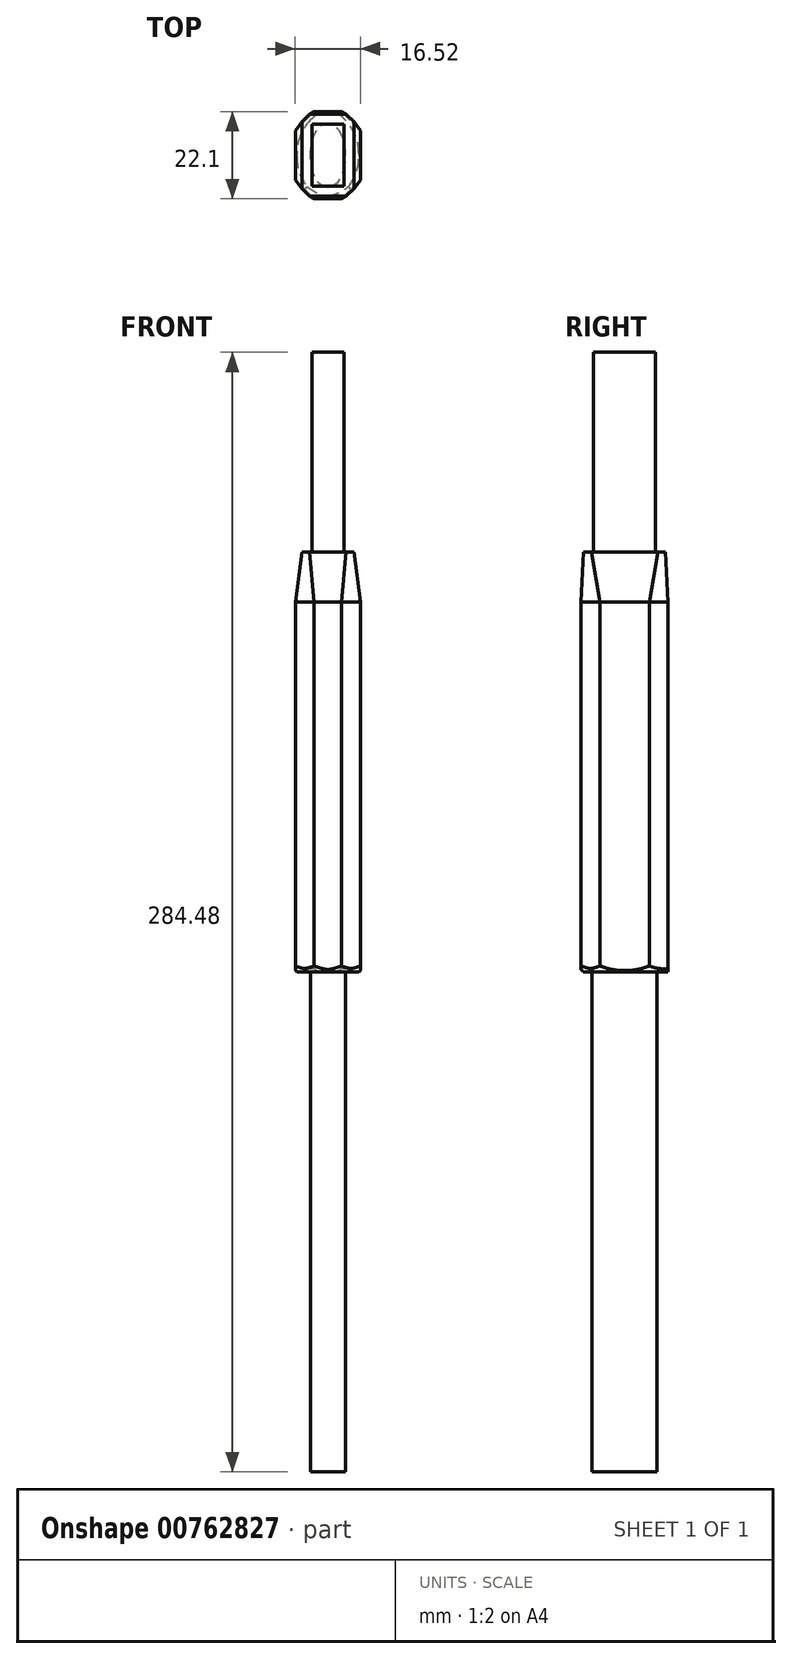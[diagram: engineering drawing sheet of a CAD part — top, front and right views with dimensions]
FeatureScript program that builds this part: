
annotation { "Feature Type Name" : "Feature", "Feature Type Description" : "" }
export const myFeature = defineFeature(function(context is Context, id is Id, definition is map)
    precondition{}
    {
        {
            var Q0;
            Q0=qCreatedBy(makeId("Top.planeOp"),FACE);
            var sketch = newSketch(context, id + "F0", { "sketchPlane" : qUnion([Q0])});
            skLineSegment(sketch, "E0.bottom", {"start": v(-8.26, -11.05) * mm, "end": v(8.26, -11.05) * mm});
            skLineSegment(sketch, "E0.top", {"start": v(-8.26, 11.05) * mm, "end": v(8.26, 11.05) * mm});
            skLineSegment(sketch, "E0.left", {"start": v(-8.26, -11.05) * mm, "end": v(-8.26, 11.05) * mm});
            skLineSegment(sketch, "E0.right", {"start": v(8.26, -11.05) * mm, "end": v(8.26, 11.05) * mm});
            skPoint(sketch, "E0.middle", {"position": v(0, 0) * mm});
            skLineSegment(sketch, "E1", {"start": v(-8.26, 6.3) * mm, "end": v(-3.5, 11.05) * mm});
            skLineSegment(sketch, "E2", {"start": v(-3.5, 11.05) * mm, "end": v(3.5, 11.05) * mm});
            skLineSegment(sketch, "E3", {"start": v(3.5, 11.05) * mm, "end": v(8.26, 6.3) * mm});
            skLineSegment(sketch, "E4", {"start": v(-8.26, -6.3) * mm, "end": v(-3.5, -11.05) * mm});
            skLineSegment(sketch, "E5", {"start": v(3.5, -11.05) * mm, "end": v(8.26, -6.3) * mm});
            skSolve(sketch);
        }
        {
            var Q0;
            {var subQ3=sQuery(id+"F0.wireOp",EDGE,"E1");Q0=makeQuery(id+"F0.imprint","IMPRINT",FACE,{"disambiguationData":[TD([[makeQuery(id+"F0.imprint","IMPRINT",EDGE,{"derivedFrom":subQ3}),-1.0]])]});}
            extrude(context, id + "F1", {"entities" : qUnion([Q0]), "depth" : 93.98 * mm, "offsetDistance" : 25.4 * mm});
        }
        {
            var Q0;
            Q0=makeQuery(id+"F1.opExtrude","CAP_FACE",FACE,{"disambiguationData":[OSD([sQuery(id+"F0.wireOp",EDGE,"E0.bottom"),sQuery(id+"F0.wireOp",EDGE,"E0.left"),sQuery(id+"F0.wireOp",EDGE,"E0.right"),sQuery(id+"F0.wireOp",EDGE,"E1"),sQuery(id+"F0.wireOp",EDGE,"E2"),sQuery(id+"F0.wireOp",EDGE,"E3"),sQuery(id+"F0.wireOp",EDGE,"E4"),sQuery(id+"F0.wireOp",EDGE,"E5")])],"isStart":false});
            cPlane(context, id + "F2", {"entities" : qUnion([Q0]), "cplaneType" : CPlaneType.OFFSET, "offset" : 12.7 * mm, "width" : 152.4 * mm, "height" : 152.4 * mm});
        }
        {
            var Q0;
            Q0=qCreatedBy(id+"F2.planeOp",FACE);
            var sketch = newSketch(context, id + "F3", { "sketchPlane" : qUnion([Q0])});
            skLineSegment(sketch, "E6.bottom", {"start": v(-6.6, -10.41) * mm, "end": v(6.6, -10.41) * mm});
            skLineSegment(sketch, "E6.top", {"start": v(-6.6, 10.41) * mm, "end": v(6.6, 10.41) * mm});
            skLineSegment(sketch, "E6.left", {"start": v(-6.6, -10.41) * mm, "end": v(-6.6, 10.41) * mm});
            skLineSegment(sketch, "E6.right", {"start": v(6.6, -10.41) * mm, "end": v(6.6, 10.41) * mm});
            skPoint(sketch, "E6.middle", {"position": v(0, 0) * mm});
            skLineSegment(sketch, "E7", {"start": v(4.67, 10.41) * mm, "end": v(6.6, 8.48) * mm});
            skLineSegment(sketch, "E8", {"start": v(-6.6, 8.48) * mm, "end": v(-4.67, 10.41) * mm});
            skLineSegment(sketch, "E9", {"start": v(-6.6, -8.48) * mm, "end": v(-4.67, -10.41) * mm});
            skLineSegment(sketch, "E10", {"start": v(4.67, -10.41) * mm, "end": v(6.6, -8.48) * mm});
            skSolve(sketch);
        }
        {
            var Q1;
            {var subQ0=sQuery(id+"F3.wireOp",EDGE,"E7");Q1=makeQuery(id+"F3.imprint","IMPRINT",FACE,{"disambiguationData":[TD([[makeQuery(id+"F3.imprint","IMPRINT",EDGE,{"derivedFrom":subQ0}),-1.0]])]});}
            var Q2;
            Q2=makeQuery(id+"F1.opExtrude","CAP_FACE",FACE,{"disambiguationData":[OSD([sQuery(id+"F0.wireOp",EDGE,"E0.bottom"),sQuery(id+"F0.wireOp",EDGE,"E0.left"),sQuery(id+"F0.wireOp",EDGE,"E0.right"),sQuery(id+"F0.wireOp",EDGE,"E1"),sQuery(id+"F0.wireOp",EDGE,"E2"),sQuery(id+"F0.wireOp",EDGE,"E3"),sQuery(id+"F0.wireOp",EDGE,"E4"),sQuery(id+"F0.wireOp",EDGE,"E5")])],"isStart":false});
            loft(context, id + "F4", {"operationType" : NewBodyOperationType.ADD, "sheetProfilesArray" : [{ "sheetProfileEntities" : qUnion([Q1]) }, { "sheetProfileEntities" : qUnion([Q2]) }]});
        }
        {
            var Q0;
            {var subQ0=sQuery(id+"F3.wireOp",EDGE,"E7");Q0=makeQuery(id+"F4.opLoft","CAP_FACE",FACE,{"disambiguationData":[OSD([makeQuery(id+"F3.imprint","IMPRINT",FACE,{"disambiguationData":[TD([[makeQuery(id+"F3.imprint","IMPRINT",EDGE,{"derivedFrom":subQ0}),-1.0]])]})])],"isStart":true});}
            var sketch = newSketch(context, id + "F5", { "sketchPlane" : qUnion([Q0])});
            skLineSegment(sketch, "E11.bottom", {"start": v(-4.06, -7.87) * mm, "end": v(4.06, -7.87) * mm});
            skLineSegment(sketch, "E11.top", {"start": v(-4.06, 7.87) * mm, "end": v(4.06, 7.87) * mm});
            skLineSegment(sketch, "E11.left", {"start": v(-4.06, -7.87) * mm, "end": v(-4.06, 7.87) * mm});
            skLineSegment(sketch, "E11.right", {"start": v(4.06, -7.87) * mm, "end": v(4.06, 7.87) * mm});
            skPoint(sketch, "E11.middle", {"position": v(0, 0) * mm});
            skSolve(sketch);
        }
        {
            var Q0;
            Q0=makeQuery(id+"F5.imprint","IMPRINT",FACE,{"disambiguationData":[TD([[makeQuery(id+"F5.imprint","IMPRINT",EDGE,{"derivedFrom":sQuery(id+"F5.wireOp",EDGE,"E11.bottom")}),1.0]])]});
            extrude(context, id + "F6", {"entities" : qUnion([Q0]), "operationType" : NewBodyOperationType.ADD, "depth" : 50.8 * mm, "offsetDistance" : 25.4 * mm});
        }
        {
            var Q0;
            Q0=makeQuery(id+"F1.opExtrude","CAP_FACE",FACE,{"disambiguationData":[OSD([sQuery(id+"F0.wireOp",EDGE,"E0.bottom"),sQuery(id+"F0.wireOp",EDGE,"E0.left"),sQuery(id+"F0.wireOp",EDGE,"E0.right"),sQuery(id+"F0.wireOp",EDGE,"E1"),sQuery(id+"F0.wireOp",EDGE,"E2"),sQuery(id+"F0.wireOp",EDGE,"E3"),sQuery(id+"F0.wireOp",EDGE,"E4"),sQuery(id+"F0.wireOp",EDGE,"E5")])],"isStart":true});
            var sketch = newSketch(context, id + "F7", { "sketchPlane" : qUnion([Q0])});
            skEllipse(sketch, "E12", {"center": v(0, 0) * mm, "majorRadius": 8.26 * mm, "minorRadius": 4.45 * mm, "majorAxis": v(0, 1)});
            skSolve(sketch);
        }
        {
            var Q0;
            Q0=makeQuery(id+"F7.imprint","IMPRINT",FACE,{"disambiguationData":[TD([[makeQuery(id+"F7.imprint","IMPRINT",EDGE,{"derivedFrom":sQuery(id+"F7.wireOp",EDGE,"E12")}),1.0]])]});
            extrude(context, id + "F8", {"entities" : qUnion([Q0]), "operationType" : NewBodyOperationType.ADD, "depth" : 127 * mm, "offsetDistance" : 25.4 * mm});
        }
        {
            var Q0;
            Q0=makeQuery(id+"F1.opExtrude","CAP_EDGE",EDGE,{"disambiguationData":[OSD([sQuery(id+"F0.wireOp",EDGE,"E4")])],"isStart":true});
            var Q1;
            Q1=makeQuery(id+"F1.opExtrude","CAP_EDGE",EDGE,{"disambiguationData":[OSD([sQuery(id+"F0.wireOp",EDGE,"E5")])],"isStart":true});
            var Q2;
            Q2=makeQuery(id+"F1.opExtrude","CAP_EDGE",EDGE,{"disambiguationData":[OSD([sQuery(id+"F0.wireOp",EDGE,"E1")])],"isStart":true});
            var Q3;
            Q3=makeQuery(id+"F1.opExtrude","CAP_EDGE",EDGE,{"disambiguationData":[OSD([sQuery(id+"F0.wireOp",EDGE,"E3")])],"isStart":true});
            chamfer(context, id + "F9", {"entities" : qUnion([Q0, Q1, Q2, Q3]), "width" : 0.84 * mm, "tangentPropagation" : true});
        }
        {
            var Q0;
            Q0=makeQuery(id+"F1.opExtrude","CAP_EDGE",EDGE,{"disambiguationData":[OSD([sQuery(id+"F0.wireOp",EDGE,"E0.bottom")])],"isStart":true});
            var Q1;
            Q1=makeQuery(id+"F1.opExtrude","CAP_EDGE",EDGE,{"disambiguationData":[OSD([sQuery(id+"F0.wireOp",EDGE,"E0.left")])],"isStart":true});
            var Q2;
            Q2=makeQuery(id+"F1.opExtrude","CAP_EDGE",EDGE,{"disambiguationData":[OSD([sQuery(id+"F0.wireOp",EDGE,"E2")])],"isStart":true});
            var Q3;
            Q3=makeQuery(id+"F1.opExtrude","CAP_EDGE",EDGE,{"disambiguationData":[OSD([sQuery(id+"F0.wireOp",EDGE,"E0.right")])],"isStart":true});
            chamfer(context, id + "F10", {"entities" : qUnion([Q0, Q1, Q2, Q3]), "width" : 0.38 * mm, "tangentPropagation" : true});
        }
        {
            var Q0;
            Q0=makeQuery(id+"F10.opChamfer","BLEND_EDGE",EDGE,{"blendedFrom":[makeQuery(id+"F1.opExtrude","CAP_EDGE",EDGE,{"disambiguationData":[OSD([sQuery(id+"F0.wireOp",EDGE,"E0.left")])],"isStart":true}),makeQuery(id+"F9.opChamfer","BLEND_FACE",FACE,{"disambiguationData":[OSD([sQuery(id+"F0.wireOp",EDGE,"E4")])]})],"blendedInto":[makeQuery(id+"F9.opChamfer","BLEND_FACE",FACE,{"disambiguationData":[OSD([sQuery(id+"F0.wireOp",EDGE,"E4")])]})]});
            var Q1;
            Q1=makeQuery(id+"F10.opChamfer","BLEND_EDGE",EDGE,{"blendedFrom":[makeQuery(id+"F1.opExtrude","CAP_EDGE",EDGE,{"disambiguationData":[OSD([sQuery(id+"F0.wireOp",EDGE,"E0.bottom")])],"isStart":true}),makeQuery(id+"F9.opChamfer","BLEND_FACE",FACE,{"disambiguationData":[OSD([sQuery(id+"F0.wireOp",EDGE,"E4")])]})],"blendedInto":[makeQuery(id+"F9.opChamfer","BLEND_FACE",FACE,{"disambiguationData":[OSD([sQuery(id+"F0.wireOp",EDGE,"E4")])]})]});
            var Q2;
            Q2=makeQuery(id+"F10.opChamfer","BLEND_EDGE",EDGE,{"blendedFrom":[makeQuery(id+"F1.opExtrude","CAP_EDGE",EDGE,{"disambiguationData":[OSD([sQuery(id+"F0.wireOp",EDGE,"E0.bottom")])],"isStart":true}),makeQuery(id+"F9.opChamfer","BLEND_FACE",FACE,{"disambiguationData":[OSD([sQuery(id+"F0.wireOp",EDGE,"E5")])]})],"blendedInto":[makeQuery(id+"F9.opChamfer","BLEND_FACE",FACE,{"disambiguationData":[OSD([sQuery(id+"F0.wireOp",EDGE,"E5")])]})]});
            var Q3;
            Q3=makeQuery(id+"F10.opChamfer","BLEND_EDGE",EDGE,{"blendedFrom":[makeQuery(id+"F1.opExtrude","CAP_EDGE",EDGE,{"disambiguationData":[OSD([sQuery(id+"F0.wireOp",EDGE,"E0.right")])],"isStart":true}),makeQuery(id+"F9.opChamfer","BLEND_FACE",FACE,{"disambiguationData":[OSD([sQuery(id+"F0.wireOp",EDGE,"E5")])]})],"blendedInto":[makeQuery(id+"F9.opChamfer","BLEND_FACE",FACE,{"disambiguationData":[OSD([sQuery(id+"F0.wireOp",EDGE,"E5")])]})]});
            var Q4;
            Q4=makeQuery(id+"F10.opChamfer","BLEND_EDGE",EDGE,{"blendedFrom":[makeQuery(id+"F1.opExtrude","CAP_EDGE",EDGE,{"disambiguationData":[OSD([sQuery(id+"F0.wireOp",EDGE,"E0.right")])],"isStart":true}),makeQuery(id+"F9.opChamfer","BLEND_FACE",FACE,{"disambiguationData":[OSD([sQuery(id+"F0.wireOp",EDGE,"E3")])]})],"blendedInto":[makeQuery(id+"F9.opChamfer","BLEND_FACE",FACE,{"disambiguationData":[OSD([sQuery(id+"F0.wireOp",EDGE,"E3")])]})]});
            var Q5;
            Q5=makeQuery(id+"F10.opChamfer","BLEND_EDGE",EDGE,{"blendedFrom":[makeQuery(id+"F1.opExtrude","CAP_EDGE",EDGE,{"disambiguationData":[OSD([sQuery(id+"F0.wireOp",EDGE,"E2")])],"isStart":true}),makeQuery(id+"F9.opChamfer","BLEND_FACE",FACE,{"disambiguationData":[OSD([sQuery(id+"F0.wireOp",EDGE,"E3")])]})],"blendedInto":[makeQuery(id+"F9.opChamfer","BLEND_FACE",FACE,{"disambiguationData":[OSD([sQuery(id+"F0.wireOp",EDGE,"E3")])]})]});
            var Q6;
            Q6=makeQuery(id+"F10.opChamfer","BLEND_EDGE",EDGE,{"blendedFrom":[makeQuery(id+"F1.opExtrude","CAP_EDGE",EDGE,{"disambiguationData":[OSD([sQuery(id+"F0.wireOp",EDGE,"E2")])],"isStart":true}),makeQuery(id+"F9.opChamfer","BLEND_FACE",FACE,{"disambiguationData":[OSD([sQuery(id+"F0.wireOp",EDGE,"E1")])]})],"blendedInto":[makeQuery(id+"F9.opChamfer","BLEND_FACE",FACE,{"disambiguationData":[OSD([sQuery(id+"F0.wireOp",EDGE,"E1")])]})]});
            var Q7;
            Q7=makeQuery(id+"F10.opChamfer","BLEND_EDGE",EDGE,{"blendedFrom":[makeQuery(id+"F1.opExtrude","CAP_EDGE",EDGE,{"disambiguationData":[OSD([sQuery(id+"F0.wireOp",EDGE,"E0.left")])],"isStart":true}),makeQuery(id+"F9.opChamfer","BLEND_FACE",FACE,{"disambiguationData":[OSD([sQuery(id+"F0.wireOp",EDGE,"E1")])]})],"blendedInto":[makeQuery(id+"F9.opChamfer","BLEND_FACE",FACE,{"disambiguationData":[OSD([sQuery(id+"F0.wireOp",EDGE,"E1")])]})]});
            fillet(context, id + "F11", {"entities" : qUnion([Q0, Q1, Q2, Q3, Q4, Q5, Q6, Q7]), "radius" : 17.78 * mm, "tangentPropagation" : true, "allowEdgeOverflow" : false});
        }
    });
